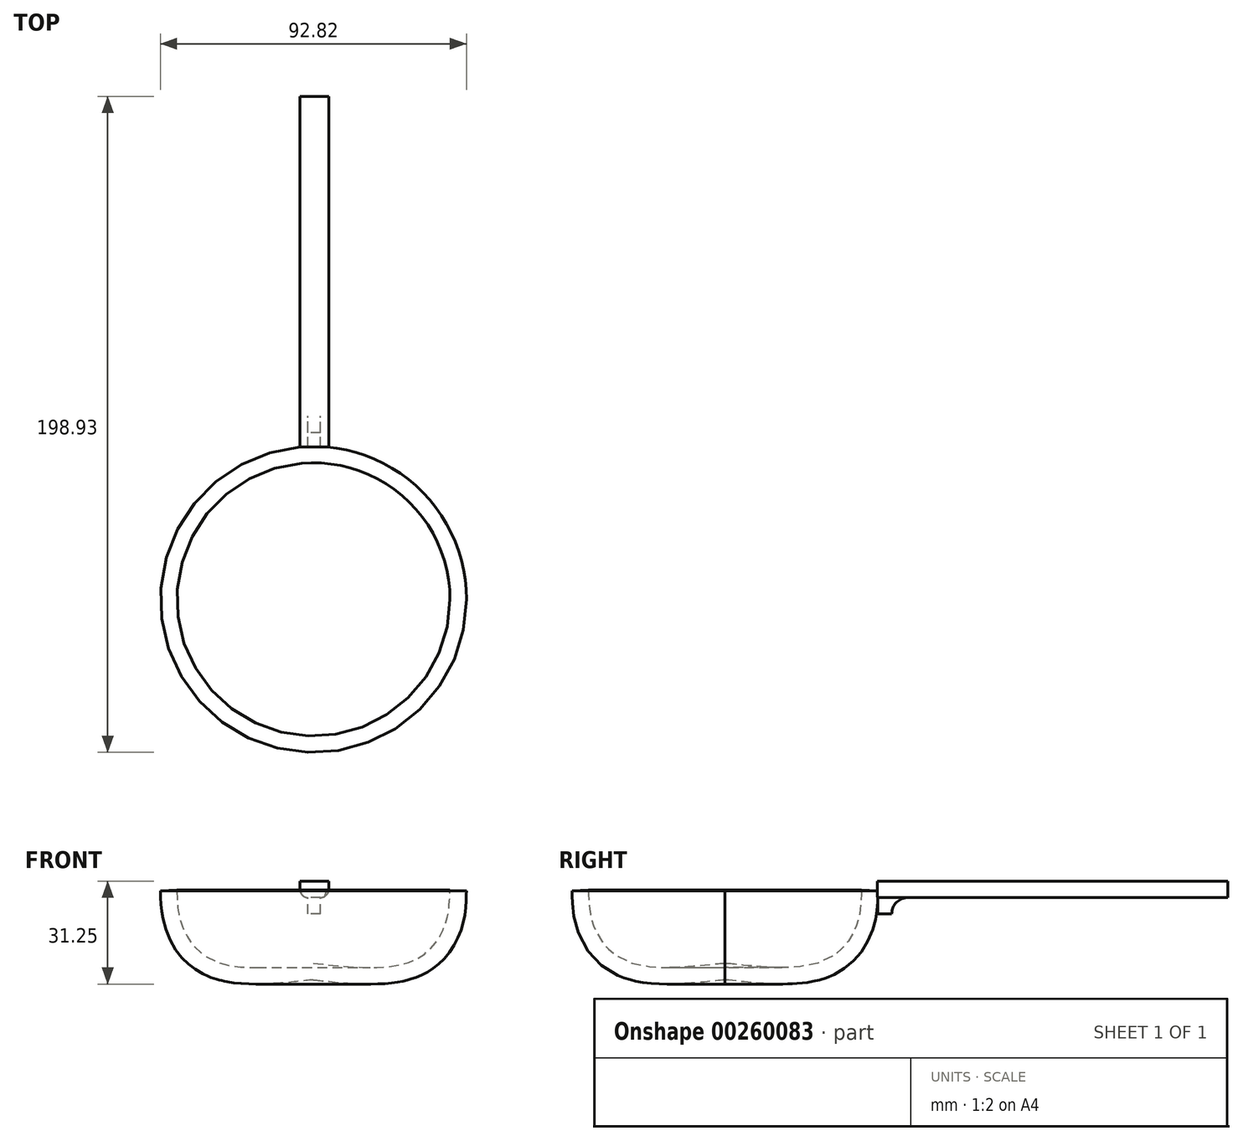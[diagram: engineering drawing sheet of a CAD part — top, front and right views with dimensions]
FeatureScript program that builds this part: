
annotation { "Feature Type Name" : "Feature", "Feature Type Description" : "" }
export const myFeature = defineFeature(function(context is Context, id is Id, definition is map)
    precondition{}
    {
        {
            var Q0;
            Q0=qCreatedBy(makeId("Front.planeOp"),FACE);
            var sketch = newSketch(context, id + "F0", { "sketchPlane" : qUnion([Q0])});
            skFitSpline(sketch, "E0", {"points": [v(0, 0) * mm, v(27.94, 0) * mm, v(40.27, 12.77) * mm, v(41.42, 22.27) * mm], "startDerivative": vector(21.73, 0) * mm, "endDerivative": vector(1.41, 36.17) * mm});
            skFitSpline(sketch, "E1.0", {"points": [v(-0.22, -5) * mm, v(-0.19, -5) * mm, v(-0.15, -5) * mm, v(-0.09, -5) * mm, v(-0.05, -5) * mm, v(-0.03, -5) * mm, v(-0.01, -5) * mm, v(0, -5) * mm, v(0, -5) * mm, v(0, -5) * mm, v(0, -5) * mm, v(0, -5) * mm, v(0, -5) * mm, v(0.03, -5) * mm, v(0.06, -5) * mm, v(0.13, -5) * mm, v(0.25, -5.01) * mm, v(0.44, -5.02) * mm, v(0.75, -5.05) * mm, v(1.22, -5.1) * mm, v(1.9, -5.16) * mm, v(2.93, -5.27) * mm, v(4.44, -5.43) * mm, v(6.54, -5.65) * mm, v(8.86, -5.86) * mm, v(11.36, -6.05) * mm, v(14, -6.18) * mm, v(16.72, -6.25) * mm, v(19.5, -6.22) * mm, v(22.27, -6.07) * mm, v(24.57, -5.81) * mm, v(26.4, -5.51) * mm, v(27.74, -5.23) * mm, v(28.85, -4.95) * mm, v(29.72, -4.68) * mm, v(31.01, -4.26) * mm, v(32.84, -3.5) * mm, v(35.06, -2.3) * mm, v(37.04, -0.9) * mm, v(39.37, 1.17) * mm, v(41.71, 4) * mm, v(43.71, 7.55) * mm, v(45.03, 11.01) * mm, v(45.82, 14.24) * mm, v(46.2, 17.2) * mm, v(46.34, 19.82) * mm, v(46.38, 21.36) * mm, v(46.41, 22.08) * mm]});
            skLineSegment(sketch, "E2", {"start": v(41.42, 22.27) * mm, "end": v(46.41, 22.06) * mm});
            skLineSegment(sketch, "E3", {"start": v(0, 0) * mm, "end": v(0, -5) * mm});
            skSolve(sketch);
        }
        {
            var Q0;
            Q0=makeQuery(id+"F0.imprint","IMPRINT",FACE,{"disambiguationData":[TD([[makeQuery(id+"F0.imprint","IMPRINT",EDGE,{"derivedFrom":sQuery(id+"F0.wireOp",EDGE,"E0")}),-1.0]])]});
            var Q1;
            Q1=sQuery(id+"F0.wireOp",EDGE,"E3");
            revolve(context, id + "F1", {"entities" : qUnion([Q0]), "axis" : qUnion([Q1]), "revolveType" : RevolveType.FULL});
        }
        {
            var Q0;
            Q0=qCreatedBy(makeId("Top.planeOp"),FACE);
            cPlane(context, id + "F2", {"entities" : qUnion([Q0]), "cplaneType" : CPlaneType.OFFSET, "offset" : 25 * mm, "width" : 150 * mm, "height" : 150 * mm});
        }
        {
            var Q0;
            Q0=qCreatedBy(id+"F2.planeOp",FACE);
            var sketch = newSketch(context, id + "F3", { "sketchPlane" : qUnion([Q0])});
            skLineSegment(sketch, "E4.bottom", {"start": v(-4.16, 46.23) * mm, "end": v(4.66, 46.23) * mm});
            skLineSegment(sketch, "E4.top", {"start": v(-4.16, 152.52) * mm, "end": v(4.66, 152.52) * mm});
            skLineSegment(sketch, "E4.left", {"start": v(-4.16, 46.23) * mm, "end": v(-4.16, 152.52) * mm});
            skLineSegment(sketch, "E4.right", {"start": v(4.66, 46.23) * mm, "end": v(4.66, 152.52) * mm});
            skSolve(sketch);
        }
        {
            var Q0;
            Q0 = qSketchRegion(id + "F3", true);
            extrude(context, id + "F4", {"entities" : qUnion([Q0]), "operationType" : NewBodyOperationType.ADD, "oppositeDirection" : true, "depth" : 5 * mm});
        }
        {
            var Q0;
            Q0=makeQuery(id+"F4.opExtrude","CAP_EDGE",EDGE,{"disambiguationData":[OSD([sQuery(id+"F3.wireOp",EDGE,"E4.right")])],"isStart":false});
            var Q1;
            Q1=makeQuery(id+"F4.opExtrude","CAP_EDGE",EDGE,{"disambiguationData":[OSD([sQuery(id+"F3.wireOp",EDGE,"E4.left")])],"isStart":false});
            fillet(context, id + "F5", {"entities" : qUnion([Q0, Q1]), "radius" : 2.5 * mm, "tangentPropagation" : true, "allowEdgeOverflow" : false});
        }
        {
            var Q0;
            Q0=makeQuery(id+"F4.opExtrude","CAP_FACE",FACE,{"disambiguationData":[OSD([sQuery(id+"F3.wireOp",EDGE,"E4.bottom"),sQuery(id+"F3.wireOp",EDGE,"E4.top"),sQuery(id+"F3.wireOp",EDGE,"E4.left"),sQuery(id+"F3.wireOp",EDGE,"E4.right")])],"isStart":false});
            var sketch = newSketch(context, id + "F6", { "sketchPlane" : qUnion([Q0])});
            skLineSegment(sketch, "E5.bottom", {"start": v(2.16, -46.29) * mm, "end": v(-1.66, -46.29) * mm});
            skLineSegment(sketch, "E5.top", {"start": v(2.16, -55.58) * mm, "end": v(-1.66, -55.58) * mm});
            skLineSegment(sketch, "E5.left", {"start": v(2.16, -46.29) * mm, "end": v(2.16, -55.58) * mm});
            skLineSegment(sketch, "E5.right", {"start": v(-1.66, -46.29) * mm, "end": v(-1.66, -55.58) * mm});
            skSolve(sketch);
        }
        {
            var Q0;
            {var subQ0=sQuery(id+"F6.wireOp",EDGE,"E5.top");Q0=makeQuery(id+"F6.imprint","IMPRINT",FACE,{"disambiguationData":[TD([[makeQuery(id+"F6.imprint","IMPRINT",EDGE,{"derivedFrom":subQ0}),-1.0]])]});}
            extrude(context, id + "F7", {"entities" : qUnion([Q0]), "operationType" : NewBodyOperationType.ADD, "depth" : 5 * mm});
        }
        {
            var Q0;
            Q0=makeQuery(id+"F7.opExtrude","SWEPT_FACE",FACE,{"disambiguationData":[OSD([sQuery(id+"F6.wireOp",EDGE,"E5.right")])]});
            var sketch = newSketch(context, id + "F8", { "sketchPlane" : qUnion([Q0])});
            skCircle(sketch, "E6", {"center": v(-55.58, 15) * mm, "radius": 5 * mm});
            skSolve(sketch);
        }
        {
            var Q0;
            Q0 = qSketchRegion(id + "F8", true);
            extrude(context, id + "F9", {"entities" : qUnion([Q0]), "operationType" : NewBodyOperationType.REMOVE, "oppositeDirection" : true, "depth" : 25 * mm});
        }
    });
